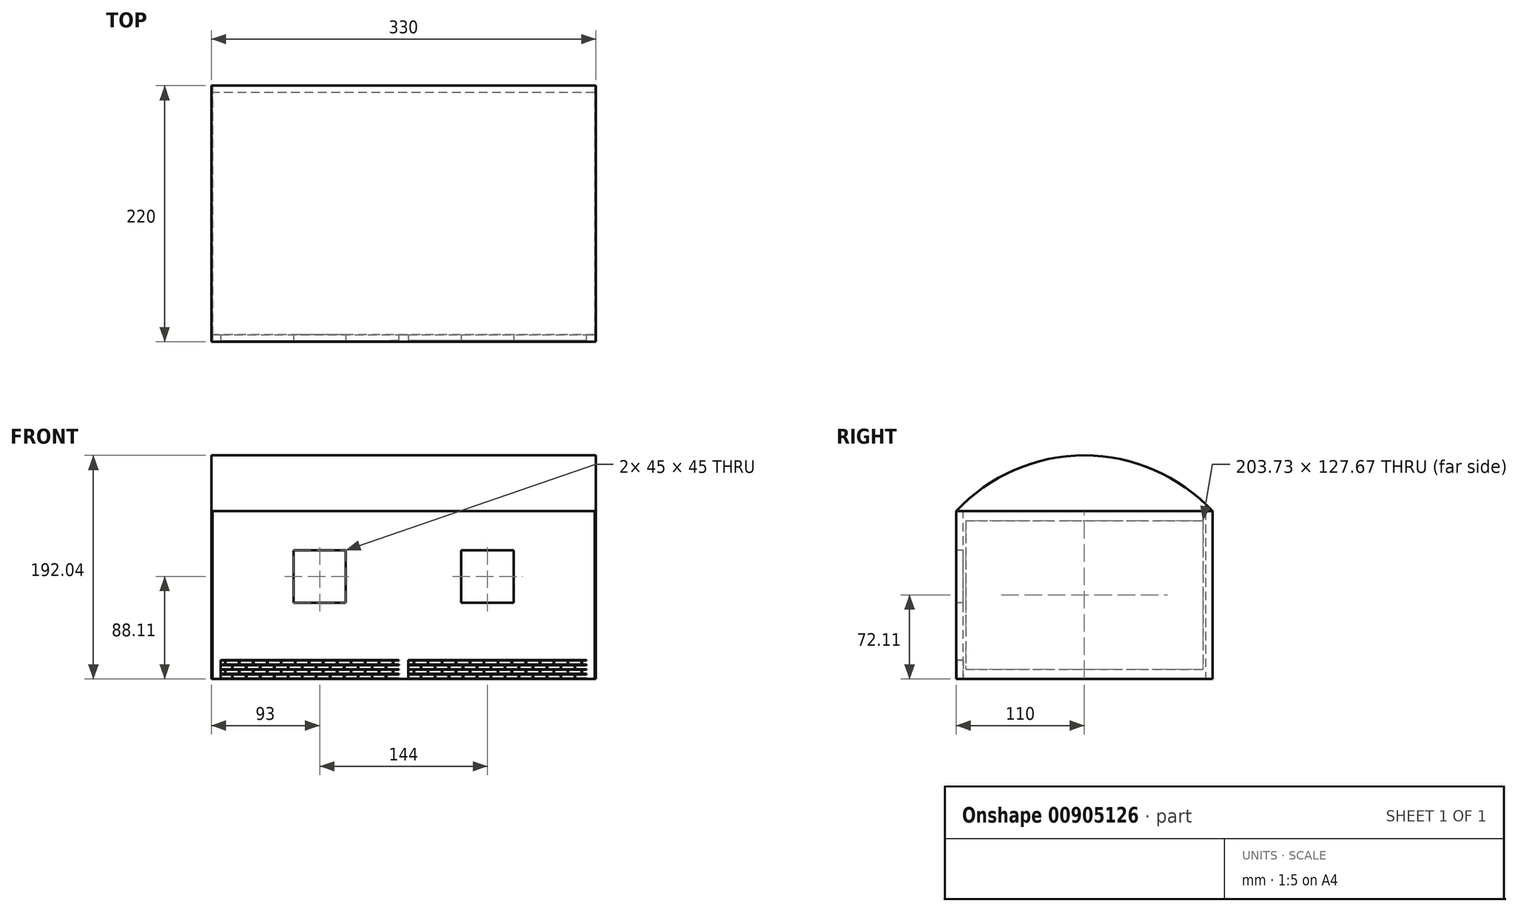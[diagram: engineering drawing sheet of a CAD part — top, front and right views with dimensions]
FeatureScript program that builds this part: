
annotation { "Feature Type Name" : "Feature", "Feature Type Description" : "" }
export const myFeature = defineFeature(function(context is Context, id is Id, definition is map)
    precondition{}
    {
        {
            var Q0;
            Q0=qCreatedBy(makeId("Front.planeOp"),FACE);
            var sketch = newSketch(context, id + "F0", { "sketchPlane" : qUnion([Q0])});
            skLineSegment(sketch, "E0", {"start": v(-165, -72) * mm, "end": v(165, -72) * mm});
            skLineSegment(sketch, "E1", {"start": v(-165, -72) * mm, "end": v(-165, 72) * mm});
            skLineSegment(sketch, "E2", {"start": v(165, -72) * mm, "end": v(165, 72) * mm});
            skLineSegment(sketch, "E3", {"start": v(165, 72) * mm, "end": v(-165, 72) * mm});
            skLineSegment(sketch, "E4", {"start": v(0, 72) * mm, "end": v(0, -56) * mm});
            skLineSegment(sketch, "E5", {"start": v(48, 72) * mm, "end": v(48, -56) * mm});
            skLineSegment(sketch, "E6", {"start": v(96, 72) * mm, "end": v(96, -56) * mm});
            skLineSegment(sketch, "E7", {"start": v(144, 72) * mm, "end": v(144, -56) * mm});
            skLineSegment(sketch, "E8", {"start": v(-48, 72) * mm, "end": v(-48, -56) * mm});
            skLineSegment(sketch, "E9", {"start": v(-96, 72) * mm, "end": v(-96, -56) * mm});
            skLineSegment(sketch, "E10", {"start": v(-144, 72) * mm, "end": v(-144, -56) * mm});
            skLineSegment(sketch, "E11", {"start": v(-165, -56) * mm, "end": v(165, -56) * mm});
            skLineSegment(sketch, "E12", {"start": v(-94.5, 38.5) * mm, "end": v(-49.5, 38.5) * mm});
            skLineSegment(sketch, "E13", {"start": v(-49.5, 38.5) * mm, "end": v(-49.5, -6.5) * mm});
            skLineSegment(sketch, "E14", {"start": v(-49.5, -6.5) * mm, "end": v(-94.5, -6.5) * mm});
            skLineSegment(sketch, "E15", {"start": v(-94.5, -6.5) * mm, "end": v(-94.5, 38.5) * mm});
            skLineSegment(sketch, "E16", {"start": v(49.5, 38.5) * mm, "end": v(94.5, 38.5) * mm});
            skLineSegment(sketch, "E17", {"start": v(94.5, 38.5) * mm, "end": v(94.5, -6.5) * mm});
            skLineSegment(sketch, "E18", {"start": v(94.5, -6.5) * mm, "end": v(49.5, -6.5) * mm});
            skLineSegment(sketch, "E19", {"start": v(49.5, -6.5) * mm, "end": v(49.5, 38.5) * mm});
            skLineSegment(sketch, "E20", {"start": v(-72, 38.5) * mm, "end": v(-72, -6.5) * mm});
            skLineSegment(sketch, "E21", {"start": v(72, 38.5) * mm, "end": v(72, -6.5) * mm});
            skLineSegment(sketch, "E22", {"start": v(-157, -56) * mm, "end": v(-157, -72) * mm});
            skLineSegment(sketch, "E23", {"start": v(-4, -56) * mm, "end": v(-4, -72) * mm});
            skLineSegment(sketch, "E24", {"start": v(-164, -72) * mm, "end": v(-164, 72) * mm});
            skLineSegment(sketch, "E25", {"start": v(164, -72) * mm, "end": v(164, 72) * mm});
            skLineSegment(sketch, "E26", {"start": v(-146.75, -68.25) * mm, "end": v(-135.25, -68.25) * mm});
            skLineSegment(sketch, "E27", {"start": v(-135.25, -68.25) * mm, "end": v(-135.25, -71.75) * mm});
            skLineSegment(sketch, "E28", {"start": v(-135.25, -71.75) * mm, "end": v(-146.75, -71.75) * mm});
            skLineSegment(sketch, "E29", {"start": v(-146.75, -71.75) * mm, "end": v(-146.75, -68.25) * mm});
            skLineSegment(sketch, "E30", {"start": v(-134.75, -68.25) * mm, "end": v(-123.25, -68.25) * mm});
            skLineSegment(sketch, "E31", {"start": v(-123.25, -68.25) * mm, "end": v(-123.25, -71.75) * mm});
            skLineSegment(sketch, "E32", {"start": v(-123.25, -71.75) * mm, "end": v(-134.75, -71.75) * mm});
            skLineSegment(sketch, "E33", {"start": v(-134.75, -71.75) * mm, "end": v(-134.75, -68.25) * mm});
            skLineSegment(sketch, "E34", {"start": v(-122.75, -68.25) * mm, "end": v(-111.25, -68.25) * mm});
            skLineSegment(sketch, "E35", {"start": v(-111.25, -68.25) * mm, "end": v(-111.25, -71.75) * mm});
            skLineSegment(sketch, "E36", {"start": v(-111.25, -71.75) * mm, "end": v(-122.75, -71.75) * mm});
            skLineSegment(sketch, "E37", {"start": v(-122.75, -71.75) * mm, "end": v(-122.75, -68.25) * mm});
            skLineSegment(sketch, "E38", {"start": v(-110.75, -68.25) * mm, "end": v(-99.25, -68.25) * mm});
            skLineSegment(sketch, "E39", {"start": v(-99.25, -68.25) * mm, "end": v(-99.25, -71.75) * mm});
            skLineSegment(sketch, "E40", {"start": v(-99.25, -71.75) * mm, "end": v(-110.75, -71.75) * mm});
            skLineSegment(sketch, "E41", {"start": v(-110.75, -71.75) * mm, "end": v(-110.75, -68.25) * mm});
            skLineSegment(sketch, "E42", {"start": v(-98.75, -68.25) * mm, "end": v(-87.25, -68.25) * mm});
            skLineSegment(sketch, "E43", {"start": v(-87.25, -68.25) * mm, "end": v(-87.25, -71.75) * mm});
            skLineSegment(sketch, "E44", {"start": v(-87.25, -71.75) * mm, "end": v(-98.75, -71.75) * mm});
            skLineSegment(sketch, "E45", {"start": v(-98.75, -71.75) * mm, "end": v(-98.75, -68.25) * mm});
            skLineSegment(sketch, "E46", {"start": v(-86.75, -68.25) * mm, "end": v(-75.25, -68.25) * mm});
            skLineSegment(sketch, "E47", {"start": v(-75.25, -68.25) * mm, "end": v(-75.25, -71.75) * mm});
            skLineSegment(sketch, "E48", {"start": v(-75.25, -71.75) * mm, "end": v(-86.75, -71.75) * mm});
            skLineSegment(sketch, "E49", {"start": v(-86.75, -71.75) * mm, "end": v(-86.75, -68.25) * mm});
            skLineSegment(sketch, "E50", {"start": v(-74.75, -68.25) * mm, "end": v(-63.25, -68.25) * mm});
            skLineSegment(sketch, "E51", {"start": v(-63.25, -68.25) * mm, "end": v(-63.25, -71.75) * mm});
            skLineSegment(sketch, "E52", {"start": v(-63.25, -71.75) * mm, "end": v(-74.75, -71.75) * mm});
            skLineSegment(sketch, "E53", {"start": v(-74.75, -71.75) * mm, "end": v(-74.75, -68.25) * mm});
            skLineSegment(sketch, "E54", {"start": v(-62.75, -68.25) * mm, "end": v(-51.25, -68.25) * mm});
            skLineSegment(sketch, "E55", {"start": v(-51.25, -68.25) * mm, "end": v(-51.25, -71.75) * mm});
            skLineSegment(sketch, "E56", {"start": v(-51.25, -71.75) * mm, "end": v(-62.75, -71.75) * mm});
            skLineSegment(sketch, "E57", {"start": v(-62.75, -71.75) * mm, "end": v(-62.75, -68.25) * mm});
            skLineSegment(sketch, "E58", {"start": v(-50.75, -68.25) * mm, "end": v(-39.25, -68.25) * mm});
            skLineSegment(sketch, "E59", {"start": v(-39.25, -68.25) * mm, "end": v(-39.25, -71.75) * mm});
            skLineSegment(sketch, "E60", {"start": v(-39.25, -71.75) * mm, "end": v(-50.75, -71.75) * mm});
            skLineSegment(sketch, "E61", {"start": v(-50.75, -71.75) * mm, "end": v(-50.75, -68.25) * mm});
            skLineSegment(sketch, "E62", {"start": v(-38.75, -68.25) * mm, "end": v(-27.25, -68.25) * mm});
            skLineSegment(sketch, "E63", {"start": v(-27.25, -68.25) * mm, "end": v(-27.25, -71.75) * mm});
            skLineSegment(sketch, "E64", {"start": v(-27.25, -71.75) * mm, "end": v(-38.75, -71.75) * mm});
            skLineSegment(sketch, "E65", {"start": v(-38.75, -71.75) * mm, "end": v(-38.75, -68.25) * mm});
            skLineSegment(sketch, "E66", {"start": v(-26.75, -68.25) * mm, "end": v(-15.25, -68.25) * mm});
            skLineSegment(sketch, "E67", {"start": v(-15.25, -68.25) * mm, "end": v(-15.25, -71.75) * mm});
            skLineSegment(sketch, "E68", {"start": v(-15.25, -71.75) * mm, "end": v(-26.75, -71.75) * mm});
            skLineSegment(sketch, "E69", {"start": v(-26.75, -71.75) * mm, "end": v(-26.75, -68.25) * mm});
            skLineSegment(sketch, "E70", {"start": v(-152.75, -64.25) * mm, "end": v(-141.25, -64.25) * mm});
            skLineSegment(sketch, "E71", {"start": v(-141.25, -64.25) * mm, "end": v(-141.25, -67.75) * mm});
            skLineSegment(sketch, "E72", {"start": v(-141.25, -67.75) * mm, "end": v(-152.75, -67.75) * mm});
            skLineSegment(sketch, "E73", {"start": v(-152.75, -67.75) * mm, "end": v(-152.75, -64.25) * mm});
            skLineSegment(sketch, "E74", {"start": v(-140.75, -64.25) * mm, "end": v(-129.25, -64.25) * mm});
            skLineSegment(sketch, "E75", {"start": v(-129.25, -64.25) * mm, "end": v(-129.25, -67.75) * mm});
            skLineSegment(sketch, "E76", {"start": v(-129.25, -67.75) * mm, "end": v(-140.75, -67.75) * mm});
            skLineSegment(sketch, "E77", {"start": v(-140.75, -67.75) * mm, "end": v(-140.75, -64.25) * mm});
            skLineSegment(sketch, "E78", {"start": v(-128.75, -64.25) * mm, "end": v(-117.25, -64.25) * mm});
            skLineSegment(sketch, "E79", {"start": v(-117.25, -64.25) * mm, "end": v(-117.25, -67.75) * mm});
            skLineSegment(sketch, "E80", {"start": v(-117.25, -67.75) * mm, "end": v(-128.75, -67.75) * mm});
            skLineSegment(sketch, "E81", {"start": v(-128.75, -67.75) * mm, "end": v(-128.75, -64.25) * mm});
            skLineSegment(sketch, "E82", {"start": v(-116.75, -64.25) * mm, "end": v(-105.25, -64.25) * mm});
            skLineSegment(sketch, "E83", {"start": v(-105.25, -64.25) * mm, "end": v(-105.25, -67.75) * mm});
            skLineSegment(sketch, "E84", {"start": v(-105.25, -67.75) * mm, "end": v(-116.75, -67.75) * mm});
            skLineSegment(sketch, "E85", {"start": v(-116.75, -67.75) * mm, "end": v(-116.75, -64.25) * mm});
            skLineSegment(sketch, "E86", {"start": v(-104.75, -64.25) * mm, "end": v(-93.25, -64.25) * mm});
            skLineSegment(sketch, "E87", {"start": v(-93.25, -64.25) * mm, "end": v(-93.25, -67.75) * mm});
            skLineSegment(sketch, "E88", {"start": v(-93.25, -67.75) * mm, "end": v(-104.75, -67.75) * mm});
            skLineSegment(sketch, "E89", {"start": v(-104.75, -67.75) * mm, "end": v(-104.75, -64.25) * mm});
            skLineSegment(sketch, "E90", {"start": v(-92.75, -64.25) * mm, "end": v(-81.25, -64.25) * mm});
            skLineSegment(sketch, "E91", {"start": v(-81.25, -64.25) * mm, "end": v(-81.25, -67.75) * mm});
            skLineSegment(sketch, "E92", {"start": v(-81.25, -67.75) * mm, "end": v(-92.75, -67.75) * mm});
            skLineSegment(sketch, "E93", {"start": v(-92.75, -67.75) * mm, "end": v(-92.75, -64.25) * mm});
            skLineSegment(sketch, "E94", {"start": v(-80.75, -64.25) * mm, "end": v(-69.25, -64.25) * mm});
            skLineSegment(sketch, "E95", {"start": v(-69.25, -64.25) * mm, "end": v(-69.25, -67.75) * mm});
            skLineSegment(sketch, "E96", {"start": v(-69.25, -67.75) * mm, "end": v(-80.75, -67.75) * mm});
            skLineSegment(sketch, "E97", {"start": v(-80.75, -67.75) * mm, "end": v(-80.75, -64.25) * mm});
            skLineSegment(sketch, "E98", {"start": v(-68.75, -64.25) * mm, "end": v(-57.25, -64.25) * mm});
            skLineSegment(sketch, "E99", {"start": v(-57.25, -64.25) * mm, "end": v(-57.25, -67.75) * mm});
            skLineSegment(sketch, "E100", {"start": v(-57.25, -67.75) * mm, "end": v(-68.75, -67.75) * mm});
            skLineSegment(sketch, "E101", {"start": v(-68.75, -67.75) * mm, "end": v(-68.75, -64.25) * mm});
            skLineSegment(sketch, "E102", {"start": v(-56.75, -64.25) * mm, "end": v(-45.25, -64.25) * mm});
            skLineSegment(sketch, "E103", {"start": v(-45.25, -64.25) * mm, "end": v(-45.25, -67.75) * mm});
            skLineSegment(sketch, "E104", {"start": v(-45.25, -67.75) * mm, "end": v(-56.75, -67.75) * mm});
            skLineSegment(sketch, "E105", {"start": v(-56.75, -67.75) * mm, "end": v(-56.75, -64.25) * mm});
            skLineSegment(sketch, "E106", {"start": v(-44.75, -64.25) * mm, "end": v(-33.25, -64.25) * mm});
            skLineSegment(sketch, "E107", {"start": v(-33.25, -64.25) * mm, "end": v(-33.25, -67.75) * mm});
            skLineSegment(sketch, "E108", {"start": v(-33.25, -67.75) * mm, "end": v(-44.75, -67.75) * mm});
            skLineSegment(sketch, "E109", {"start": v(-44.75, -67.75) * mm, "end": v(-44.75, -64.25) * mm});
            skLineSegment(sketch, "E110", {"start": v(-32.75, -64.25) * mm, "end": v(-21.25, -64.25) * mm});
            skLineSegment(sketch, "E111", {"start": v(-21.25, -64.25) * mm, "end": v(-21.25, -67.75) * mm});
            skLineSegment(sketch, "E112", {"start": v(-21.25, -67.75) * mm, "end": v(-32.75, -67.75) * mm});
            skLineSegment(sketch, "E113", {"start": v(-32.75, -67.75) * mm, "end": v(-32.75, -64.25) * mm});
            skLineSegment(sketch, "E114", {"start": v(-20.75, -64.25) * mm, "end": v(-9.25, -64.25) * mm});
            skLineSegment(sketch, "E115", {"start": v(-9.25, -64.25) * mm, "end": v(-9.25, -67.75) * mm});
            skLineSegment(sketch, "E116", {"start": v(-9.25, -67.75) * mm, "end": v(-20.75, -67.75) * mm});
            skLineSegment(sketch, "E117", {"start": v(-20.75, -67.75) * mm, "end": v(-20.75, -64.25) * mm});
            skLineSegment(sketch, "E118", {"start": v(-146.75, -60.25) * mm, "end": v(-135.25, -60.25) * mm});
            skLineSegment(sketch, "E119", {"start": v(-135.25, -60.25) * mm, "end": v(-135.25, -63.75) * mm});
            skLineSegment(sketch, "E120", {"start": v(-135.25, -63.75) * mm, "end": v(-146.75, -63.75) * mm});
            skLineSegment(sketch, "E121", {"start": v(-146.75, -63.75) * mm, "end": v(-146.75, -60.25) * mm});
            skLineSegment(sketch, "E122", {"start": v(-134.75, -60.25) * mm, "end": v(-123.25, -60.25) * mm});
            skLineSegment(sketch, "E123", {"start": v(-123.25, -60.25) * mm, "end": v(-123.25, -63.75) * mm});
            skLineSegment(sketch, "E124", {"start": v(-123.25, -63.75) * mm, "end": v(-134.75, -63.75) * mm});
            skLineSegment(sketch, "E125", {"start": v(-134.75, -63.75) * mm, "end": v(-134.75, -60.25) * mm});
            skLineSegment(sketch, "E126", {"start": v(-122.75, -60.25) * mm, "end": v(-111.25, -60.25) * mm});
            skLineSegment(sketch, "E127", {"start": v(-111.25, -60.25) * mm, "end": v(-111.25, -63.75) * mm});
            skLineSegment(sketch, "E128", {"start": v(-111.25, -63.75) * mm, "end": v(-122.75, -63.75) * mm});
            skLineSegment(sketch, "E129", {"start": v(-122.75, -63.75) * mm, "end": v(-122.75, -60.25) * mm});
            skLineSegment(sketch, "E130", {"start": v(-110.75, -60.25) * mm, "end": v(-99.25, -60.25) * mm});
            skLineSegment(sketch, "E131", {"start": v(-99.25, -60.25) * mm, "end": v(-99.25, -63.75) * mm});
            skLineSegment(sketch, "E132", {"start": v(-99.25, -63.75) * mm, "end": v(-110.75, -63.75) * mm});
            skLineSegment(sketch, "E133", {"start": v(-110.75, -63.75) * mm, "end": v(-110.75, -60.25) * mm});
            skLineSegment(sketch, "E134", {"start": v(-98.75, -60.25) * mm, "end": v(-87.25, -60.25) * mm});
            skLineSegment(sketch, "E135", {"start": v(-87.25, -60.25) * mm, "end": v(-87.25, -63.75) * mm});
            skLineSegment(sketch, "E136", {"start": v(-87.25, -63.75) * mm, "end": v(-98.75, -63.75) * mm});
            skLineSegment(sketch, "E137", {"start": v(-98.75, -63.75) * mm, "end": v(-98.75, -60.25) * mm});
            skLineSegment(sketch, "E138", {"start": v(-86.75, -60.25) * mm, "end": v(-75.25, -60.25) * mm});
            skLineSegment(sketch, "E139", {"start": v(-75.25, -60.25) * mm, "end": v(-75.25, -63.75) * mm});
            skLineSegment(sketch, "E140", {"start": v(-75.25, -63.75) * mm, "end": v(-86.75, -63.75) * mm});
            skLineSegment(sketch, "E141", {"start": v(-86.75, -63.75) * mm, "end": v(-86.75, -60.25) * mm});
            skLineSegment(sketch, "E142", {"start": v(-74.75, -60.25) * mm, "end": v(-63.25, -60.25) * mm});
            skLineSegment(sketch, "E143", {"start": v(-63.25, -60.25) * mm, "end": v(-63.25, -63.75) * mm});
            skLineSegment(sketch, "E144", {"start": v(-63.25, -63.75) * mm, "end": v(-74.75, -63.75) * mm});
            skLineSegment(sketch, "E145", {"start": v(-74.75, -63.75) * mm, "end": v(-74.75, -60.25) * mm});
            skLineSegment(sketch, "E146", {"start": v(-62.75, -60.25) * mm, "end": v(-51.25, -60.25) * mm});
            skLineSegment(sketch, "E147", {"start": v(-51.25, -60.25) * mm, "end": v(-51.25, -63.75) * mm});
            skLineSegment(sketch, "E148", {"start": v(-51.25, -63.75) * mm, "end": v(-62.75, -63.75) * mm});
            skLineSegment(sketch, "E149", {"start": v(-62.75, -63.75) * mm, "end": v(-62.75, -60.25) * mm});
            skLineSegment(sketch, "E150", {"start": v(-50.75, -60.25) * mm, "end": v(-39.25, -60.25) * mm});
            skLineSegment(sketch, "E151", {"start": v(-39.25, -60.25) * mm, "end": v(-39.25, -63.75) * mm});
            skLineSegment(sketch, "E152", {"start": v(-39.25, -63.75) * mm, "end": v(-50.75, -63.75) * mm});
            skLineSegment(sketch, "E153", {"start": v(-50.75, -63.75) * mm, "end": v(-50.75, -60.25) * mm});
            skLineSegment(sketch, "E154", {"start": v(-38.75, -60.25) * mm, "end": v(-27.25, -60.25) * mm});
            skLineSegment(sketch, "E155", {"start": v(-27.25, -60.25) * mm, "end": v(-27.25, -63.75) * mm});
            skLineSegment(sketch, "E156", {"start": v(-27.25, -63.75) * mm, "end": v(-38.75, -63.75) * mm});
            skLineSegment(sketch, "E157", {"start": v(-38.75, -63.75) * mm, "end": v(-38.75, -60.25) * mm});
            skLineSegment(sketch, "E158", {"start": v(-26.75, -60.25) * mm, "end": v(-15.25, -60.25) * mm});
            skLineSegment(sketch, "E159", {"start": v(-15.25, -60.25) * mm, "end": v(-15.25, -63.75) * mm});
            skLineSegment(sketch, "E160", {"start": v(-15.25, -63.75) * mm, "end": v(-26.75, -63.75) * mm});
            skLineSegment(sketch, "E161", {"start": v(-26.75, -63.75) * mm, "end": v(-26.75, -60.25) * mm});
            skLineSegment(sketch, "E162", {"start": v(-152.75, -56.25) * mm, "end": v(-141.25, -56.25) * mm});
            skLineSegment(sketch, "E163", {"start": v(-141.25, -56.25) * mm, "end": v(-141.25, -59.75) * mm});
            skLineSegment(sketch, "E164", {"start": v(-141.25, -59.75) * mm, "end": v(-152.75, -59.75) * mm});
            skLineSegment(sketch, "E165", {"start": v(-152.75, -59.75) * mm, "end": v(-152.75, -56.25) * mm});
            skLineSegment(sketch, "E166", {"start": v(-140.75, -56.25) * mm, "end": v(-129.25, -56.25) * mm});
            skLineSegment(sketch, "E167", {"start": v(-129.25, -56.25) * mm, "end": v(-129.25, -59.75) * mm});
            skLineSegment(sketch, "E168", {"start": v(-129.25, -59.75) * mm, "end": v(-140.75, -59.75) * mm});
            skLineSegment(sketch, "E169", {"start": v(-140.75, -59.75) * mm, "end": v(-140.75, -56.25) * mm});
            skLineSegment(sketch, "E170", {"start": v(-128.75, -56.25) * mm, "end": v(-117.25, -56.25) * mm});
            skLineSegment(sketch, "E171", {"start": v(-117.25, -56.25) * mm, "end": v(-117.25, -59.75) * mm});
            skLineSegment(sketch, "E172", {"start": v(-117.25, -59.75) * mm, "end": v(-128.75, -59.75) * mm});
            skLineSegment(sketch, "E173", {"start": v(-128.75, -59.75) * mm, "end": v(-128.75, -56.25) * mm});
            skLineSegment(sketch, "E174", {"start": v(-116.75, -56.25) * mm, "end": v(-105.25, -56.25) * mm});
            skLineSegment(sketch, "E175", {"start": v(-105.25, -56.25) * mm, "end": v(-105.25, -59.75) * mm});
            skLineSegment(sketch, "E176", {"start": v(-105.25, -59.75) * mm, "end": v(-116.75, -59.75) * mm});
            skLineSegment(sketch, "E177", {"start": v(-116.75, -59.75) * mm, "end": v(-116.75, -56.25) * mm});
            skLineSegment(sketch, "E178", {"start": v(-104.75, -56.25) * mm, "end": v(-93.25, -56.25) * mm});
            skLineSegment(sketch, "E179", {"start": v(-93.25, -56.25) * mm, "end": v(-93.25, -59.75) * mm});
            skLineSegment(sketch, "E180", {"start": v(-93.25, -59.75) * mm, "end": v(-104.75, -59.75) * mm});
            skLineSegment(sketch, "E181", {"start": v(-104.75, -59.75) * mm, "end": v(-104.75, -56.25) * mm});
            skLineSegment(sketch, "E182", {"start": v(-92.75, -56.25) * mm, "end": v(-81.25, -56.25) * mm});
            skLineSegment(sketch, "E183", {"start": v(-81.25, -56.25) * mm, "end": v(-81.25, -59.75) * mm});
            skLineSegment(sketch, "E184", {"start": v(-81.25, -59.75) * mm, "end": v(-92.75, -59.75) * mm});
            skLineSegment(sketch, "E185", {"start": v(-92.75, -59.75) * mm, "end": v(-92.75, -56.25) * mm});
            skLineSegment(sketch, "E186", {"start": v(-80.75, -56.25) * mm, "end": v(-69.25, -56.25) * mm});
            skLineSegment(sketch, "E187", {"start": v(-69.25, -56.25) * mm, "end": v(-69.25, -59.75) * mm});
            skLineSegment(sketch, "E188", {"start": v(-69.25, -59.75) * mm, "end": v(-80.75, -59.75) * mm});
            skLineSegment(sketch, "E189", {"start": v(-80.75, -59.75) * mm, "end": v(-80.75, -56.25) * mm});
            skLineSegment(sketch, "E190", {"start": v(-68.75, -56.25) * mm, "end": v(-57.25, -56.25) * mm});
            skLineSegment(sketch, "E191", {"start": v(-57.25, -56.25) * mm, "end": v(-57.25, -59.75) * mm});
            skLineSegment(sketch, "E192", {"start": v(-57.25, -59.75) * mm, "end": v(-68.75, -59.75) * mm});
            skLineSegment(sketch, "E193", {"start": v(-68.75, -59.75) * mm, "end": v(-68.75, -56.25) * mm});
            skLineSegment(sketch, "E194", {"start": v(-56.75, -56.25) * mm, "end": v(-45.25, -56.25) * mm});
            skLineSegment(sketch, "E195", {"start": v(-45.25, -56.25) * mm, "end": v(-45.25, -59.75) * mm});
            skLineSegment(sketch, "E196", {"start": v(-45.25, -59.75) * mm, "end": v(-56.75, -59.75) * mm});
            skLineSegment(sketch, "E197", {"start": v(-56.75, -59.75) * mm, "end": v(-56.75, -56.25) * mm});
            skLineSegment(sketch, "E198", {"start": v(-44.75, -56.25) * mm, "end": v(-33.25, -56.25) * mm});
            skLineSegment(sketch, "E199", {"start": v(-33.25, -56.25) * mm, "end": v(-33.25, -59.75) * mm});
            skLineSegment(sketch, "E200", {"start": v(-33.25, -59.75) * mm, "end": v(-44.75, -59.75) * mm});
            skLineSegment(sketch, "E201", {"start": v(-44.75, -59.75) * mm, "end": v(-44.75, -56.25) * mm});
            skLineSegment(sketch, "E202", {"start": v(-32.75, -56.25) * mm, "end": v(-21.25, -56.25) * mm});
            skLineSegment(sketch, "E203", {"start": v(-21.25, -56.25) * mm, "end": v(-21.25, -59.75) * mm});
            skLineSegment(sketch, "E204", {"start": v(-21.25, -59.75) * mm, "end": v(-32.75, -59.75) * mm});
            skLineSegment(sketch, "E205", {"start": v(-32.75, -59.75) * mm, "end": v(-32.75, -56.25) * mm});
            skLineSegment(sketch, "E206", {"start": v(-20.75, -56.25) * mm, "end": v(-9.25, -56.25) * mm});
            skLineSegment(sketch, "E207", {"start": v(-9.25, -56.25) * mm, "end": v(-9.25, -59.75) * mm});
            skLineSegment(sketch, "E208", {"start": v(-9.25, -59.75) * mm, "end": v(-20.75, -59.75) * mm});
            skLineSegment(sketch, "E209", {"start": v(-20.75, -59.75) * mm, "end": v(-20.75, -56.25) * mm});
            skLineSegment(sketch, "E210", {"start": v(-4, -67.75) * mm, "end": v(-8.75, -67.75) * mm});
            skLineSegment(sketch, "E211", {"start": v(-8.75, -67.75) * mm, "end": v(-8.75, -64.25) * mm});
            skLineSegment(sketch, "E212", {"start": v(-8.75, -64.25) * mm, "end": v(-4, -64.25) * mm});
            skLineSegment(sketch, "E213", {"start": v(-4, -71.75) * mm, "end": v(-14.75, -71.75) * mm});
            skLineSegment(sketch, "E214", {"start": v(-14.75, -71.75) * mm, "end": v(-14.75, -68.25) * mm});
            skLineSegment(sketch, "E215", {"start": v(-14.75, -68.25) * mm, "end": v(-4, -68.25) * mm});
            skLineSegment(sketch, "E216", {"start": v(-4, -63.75) * mm, "end": v(-14.75, -63.75) * mm});
            skLineSegment(sketch, "E217", {"start": v(-14.75, -63.75) * mm, "end": v(-14.75, -60.25) * mm});
            skLineSegment(sketch, "E218", {"start": v(-14.75, -60.25) * mm, "end": v(-4, -60.25) * mm});
            skLineSegment(sketch, "E219", {"start": v(-4, -59.75) * mm, "end": v(-8.75, -59.75) * mm});
            skLineSegment(sketch, "E220", {"start": v(-8.75, -59.75) * mm, "end": v(-8.75, -56.25) * mm});
            skLineSegment(sketch, "E221", {"start": v(-8.75, -56.25) * mm, "end": v(-4, -56.25) * mm});
            skLineSegment(sketch, "E222", {"start": v(-157, -56.25) * mm, "end": v(-153.25, -56.25) * mm});
            skLineSegment(sketch, "E223", {"start": v(-153.25, -56.25) * mm, "end": v(-153.25, -59.75) * mm});
            skLineSegment(sketch, "E224", {"start": v(-153.25, -59.75) * mm, "end": v(-157, -59.75) * mm});
            skLineSegment(sketch, "E225", {"start": v(-157, -60.25) * mm, "end": v(-147.25, -60.25) * mm});
            skLineSegment(sketch, "E226", {"start": v(-147.25, -60.25) * mm, "end": v(-147.25, -63.75) * mm});
            skLineSegment(sketch, "E227", {"start": v(-147.25, -63.75) * mm, "end": v(-157, -63.75) * mm});
            skLineSegment(sketch, "E228", {"start": v(-157, -64.25) * mm, "end": v(-153.25, -64.25) * mm});
            skLineSegment(sketch, "E229", {"start": v(-153.25, -64.25) * mm, "end": v(-153.25, -67.75) * mm});
            skLineSegment(sketch, "E230", {"start": v(-153.25, -67.75) * mm, "end": v(-157, -67.75) * mm});
            skLineSegment(sketch, "E231", {"start": v(-157, -68.25) * mm, "end": v(-147.25, -68.25) * mm});
            skLineSegment(sketch, "E232", {"start": v(-147.25, -68.25) * mm, "end": v(-147.25, -71.75) * mm});
            skLineSegment(sketch, "E233", {"start": v(-147.25, -71.75) * mm, "end": v(-157, -71.75) * mm});
            skLineSegment(sketch, "E234", {"start": v(157, -56) * mm, "end": v(157, -72) * mm});
            skLineSegment(sketch, "E235", {"start": v(4, -56) * mm, "end": v(4, -72) * mm});
            skLineSegment(sketch, "E236", {"start": v(146.75, -68.25) * mm, "end": v(135.25, -68.25) * mm});
            skLineSegment(sketch, "E237", {"start": v(135.25, -68.25) * mm, "end": v(135.25, -71.75) * mm});
            skLineSegment(sketch, "E238", {"start": v(135.25, -71.75) * mm, "end": v(146.75, -71.75) * mm});
            skLineSegment(sketch, "E239", {"start": v(146.75, -71.75) * mm, "end": v(146.75, -68.25) * mm});
            skLineSegment(sketch, "E240", {"start": v(134.75, -68.25) * mm, "end": v(123.25, -68.25) * mm});
            skLineSegment(sketch, "E241", {"start": v(123.25, -68.25) * mm, "end": v(123.25, -71.75) * mm});
            skLineSegment(sketch, "E242", {"start": v(123.25, -71.75) * mm, "end": v(134.75, -71.75) * mm});
            skLineSegment(sketch, "E243", {"start": v(134.75, -71.75) * mm, "end": v(134.75, -68.25) * mm});
            skLineSegment(sketch, "E244", {"start": v(122.75, -68.25) * mm, "end": v(111.25, -68.25) * mm});
            skLineSegment(sketch, "E245", {"start": v(111.25, -68.25) * mm, "end": v(111.25, -71.75) * mm});
            skLineSegment(sketch, "E246", {"start": v(111.25, -71.75) * mm, "end": v(122.75, -71.75) * mm});
            skLineSegment(sketch, "E247", {"start": v(122.75, -71.75) * mm, "end": v(122.75, -68.25) * mm});
            skLineSegment(sketch, "E248", {"start": v(110.75, -68.25) * mm, "end": v(99.25, -68.25) * mm});
            skLineSegment(sketch, "E249", {"start": v(99.25, -68.25) * mm, "end": v(99.25, -71.75) * mm});
            skLineSegment(sketch, "E250", {"start": v(99.25, -71.75) * mm, "end": v(110.75, -71.75) * mm});
            skLineSegment(sketch, "E251", {"start": v(110.75, -71.75) * mm, "end": v(110.75, -68.25) * mm});
            skLineSegment(sketch, "E252", {"start": v(98.75, -68.25) * mm, "end": v(87.25, -68.25) * mm});
            skLineSegment(sketch, "E253", {"start": v(87.25, -68.25) * mm, "end": v(87.25, -71.75) * mm});
            skLineSegment(sketch, "E254", {"start": v(87.25, -71.75) * mm, "end": v(98.75, -71.75) * mm});
            skLineSegment(sketch, "E255", {"start": v(98.75, -71.75) * mm, "end": v(98.75, -68.25) * mm});
            skLineSegment(sketch, "E256", {"start": v(86.75, -68.25) * mm, "end": v(75.25, -68.25) * mm});
            skLineSegment(sketch, "E257", {"start": v(75.25, -68.25) * mm, "end": v(75.25, -71.75) * mm});
            skLineSegment(sketch, "E258", {"start": v(75.25, -71.75) * mm, "end": v(86.75, -71.75) * mm});
            skLineSegment(sketch, "E259", {"start": v(86.75, -71.75) * mm, "end": v(86.75, -68.25) * mm});
            skLineSegment(sketch, "E260", {"start": v(74.75, -68.25) * mm, "end": v(63.25, -68.25) * mm});
            skLineSegment(sketch, "E261", {"start": v(63.25, -68.25) * mm, "end": v(63.25, -71.75) * mm});
            skLineSegment(sketch, "E262", {"start": v(63.25, -71.75) * mm, "end": v(74.75, -71.75) * mm});
            skLineSegment(sketch, "E263", {"start": v(74.75, -71.75) * mm, "end": v(74.75, -68.25) * mm});
            skLineSegment(sketch, "E264", {"start": v(62.75, -68.25) * mm, "end": v(51.25, -68.25) * mm});
            skLineSegment(sketch, "E265", {"start": v(51.25, -68.25) * mm, "end": v(51.25, -71.75) * mm});
            skLineSegment(sketch, "E266", {"start": v(51.25, -71.75) * mm, "end": v(62.75, -71.75) * mm});
            skLineSegment(sketch, "E267", {"start": v(62.75, -71.75) * mm, "end": v(62.75, -68.25) * mm});
            skLineSegment(sketch, "E268", {"start": v(50.75, -68.25) * mm, "end": v(39.25, -68.25) * mm});
            skLineSegment(sketch, "E269", {"start": v(39.25, -68.25) * mm, "end": v(39.25, -71.75) * mm});
            skLineSegment(sketch, "E270", {"start": v(39.25, -71.75) * mm, "end": v(50.75, -71.75) * mm});
            skLineSegment(sketch, "E271", {"start": v(50.75, -71.75) * mm, "end": v(50.75, -68.25) * mm});
            skLineSegment(sketch, "E272", {"start": v(38.75, -68.25) * mm, "end": v(27.25, -68.25) * mm});
            skLineSegment(sketch, "E273", {"start": v(27.25, -68.25) * mm, "end": v(27.25, -71.75) * mm});
            skLineSegment(sketch, "E274", {"start": v(27.25, -71.75) * mm, "end": v(38.75, -71.75) * mm});
            skLineSegment(sketch, "E275", {"start": v(38.75, -71.75) * mm, "end": v(38.75, -68.25) * mm});
            skLineSegment(sketch, "E276", {"start": v(26.75, -68.25) * mm, "end": v(15.25, -68.25) * mm});
            skLineSegment(sketch, "E277", {"start": v(15.25, -68.25) * mm, "end": v(15.25, -71.75) * mm});
            skLineSegment(sketch, "E278", {"start": v(15.25, -71.75) * mm, "end": v(26.75, -71.75) * mm});
            skLineSegment(sketch, "E279", {"start": v(26.75, -71.75) * mm, "end": v(26.75, -68.25) * mm});
            skLineSegment(sketch, "E280", {"start": v(152.75, -64.25) * mm, "end": v(141.25, -64.25) * mm});
            skLineSegment(sketch, "E281", {"start": v(141.25, -64.25) * mm, "end": v(141.25, -67.75) * mm});
            skLineSegment(sketch, "E282", {"start": v(141.25, -67.75) * mm, "end": v(152.75, -67.75) * mm});
            skLineSegment(sketch, "E283", {"start": v(152.75, -67.75) * mm, "end": v(152.75, -64.25) * mm});
            skLineSegment(sketch, "E284", {"start": v(140.75, -64.25) * mm, "end": v(129.25, -64.25) * mm});
            skLineSegment(sketch, "E285", {"start": v(129.25, -64.25) * mm, "end": v(129.25, -67.75) * mm});
            skLineSegment(sketch, "E286", {"start": v(129.25, -67.75) * mm, "end": v(140.75, -67.75) * mm});
            skLineSegment(sketch, "E287", {"start": v(140.75, -67.75) * mm, "end": v(140.75, -64.25) * mm});
            skLineSegment(sketch, "E288", {"start": v(128.75, -64.25) * mm, "end": v(117.25, -64.25) * mm});
            skLineSegment(sketch, "E289", {"start": v(117.25, -64.25) * mm, "end": v(117.25, -67.75) * mm});
            skLineSegment(sketch, "E290", {"start": v(117.25, -67.75) * mm, "end": v(128.75, -67.75) * mm});
            skLineSegment(sketch, "E291", {"start": v(128.75, -67.75) * mm, "end": v(128.75, -64.25) * mm});
            skLineSegment(sketch, "E292", {"start": v(116.75, -64.25) * mm, "end": v(105.25, -64.25) * mm});
            skLineSegment(sketch, "E293", {"start": v(105.25, -64.25) * mm, "end": v(105.25, -67.75) * mm});
            skLineSegment(sketch, "E294", {"start": v(105.25, -67.75) * mm, "end": v(116.75, -67.75) * mm});
            skLineSegment(sketch, "E295", {"start": v(116.75, -67.75) * mm, "end": v(116.75, -64.25) * mm});
            skLineSegment(sketch, "E296", {"start": v(104.75, -64.25) * mm, "end": v(93.25, -64.25) * mm});
            skLineSegment(sketch, "E297", {"start": v(93.25, -64.25) * mm, "end": v(93.25, -67.75) * mm});
            skLineSegment(sketch, "E298", {"start": v(93.25, -67.75) * mm, "end": v(104.75, -67.75) * mm});
            skLineSegment(sketch, "E299", {"start": v(104.75, -67.75) * mm, "end": v(104.75, -64.25) * mm});
            skLineSegment(sketch, "E300", {"start": v(92.75, -64.25) * mm, "end": v(81.25, -64.25) * mm});
            skLineSegment(sketch, "E301", {"start": v(81.25, -64.25) * mm, "end": v(81.25, -67.75) * mm});
            skLineSegment(sketch, "E302", {"start": v(81.25, -67.75) * mm, "end": v(92.75, -67.75) * mm});
            skLineSegment(sketch, "E303", {"start": v(92.75, -67.75) * mm, "end": v(92.75, -64.25) * mm});
            skLineSegment(sketch, "E304", {"start": v(80.75, -64.25) * mm, "end": v(69.25, -64.25) * mm});
            skLineSegment(sketch, "E305", {"start": v(69.25, -64.25) * mm, "end": v(69.25, -67.75) * mm});
            skLineSegment(sketch, "E306", {"start": v(69.25, -67.75) * mm, "end": v(80.75, -67.75) * mm});
            skLineSegment(sketch, "E307", {"start": v(80.75, -67.75) * mm, "end": v(80.75, -64.25) * mm});
            skLineSegment(sketch, "E308", {"start": v(68.75, -64.25) * mm, "end": v(57.25, -64.25) * mm});
            skLineSegment(sketch, "E309", {"start": v(57.25, -64.25) * mm, "end": v(57.25, -67.75) * mm});
            skLineSegment(sketch, "E310", {"start": v(57.25, -67.75) * mm, "end": v(68.75, -67.75) * mm});
            skLineSegment(sketch, "E311", {"start": v(68.75, -67.75) * mm, "end": v(68.75, -64.25) * mm});
            skLineSegment(sketch, "E312", {"start": v(56.75, -64.25) * mm, "end": v(45.25, -64.25) * mm});
            skLineSegment(sketch, "E313", {"start": v(45.25, -64.25) * mm, "end": v(45.25, -67.75) * mm});
            skLineSegment(sketch, "E314", {"start": v(45.25, -67.75) * mm, "end": v(56.75, -67.75) * mm});
            skLineSegment(sketch, "E315", {"start": v(56.75, -67.75) * mm, "end": v(56.75, -64.25) * mm});
            skLineSegment(sketch, "E316", {"start": v(44.75, -64.25) * mm, "end": v(33.25, -64.25) * mm});
            skLineSegment(sketch, "E317", {"start": v(33.25, -64.25) * mm, "end": v(33.25, -67.75) * mm});
            skLineSegment(sketch, "E318", {"start": v(33.25, -67.75) * mm, "end": v(44.75, -67.75) * mm});
            skLineSegment(sketch, "E319", {"start": v(44.75, -67.75) * mm, "end": v(44.75, -64.25) * mm});
            skLineSegment(sketch, "E320", {"start": v(32.75, -64.25) * mm, "end": v(21.25, -64.25) * mm});
            skLineSegment(sketch, "E321", {"start": v(21.25, -64.25) * mm, "end": v(21.25, -67.75) * mm});
            skLineSegment(sketch, "E322", {"start": v(21.25, -67.75) * mm, "end": v(32.75, -67.75) * mm});
            skLineSegment(sketch, "E323", {"start": v(32.75, -67.75) * mm, "end": v(32.75, -64.25) * mm});
            skLineSegment(sketch, "E324", {"start": v(20.75, -64.25) * mm, "end": v(9.25, -64.25) * mm});
            skLineSegment(sketch, "E325", {"start": v(9.25, -64.25) * mm, "end": v(9.25, -67.75) * mm});
            skLineSegment(sketch, "E326", {"start": v(9.25, -67.75) * mm, "end": v(20.75, -67.75) * mm});
            skLineSegment(sketch, "E327", {"start": v(20.75, -67.75) * mm, "end": v(20.75, -64.25) * mm});
            skLineSegment(sketch, "E328", {"start": v(146.75, -60.25) * mm, "end": v(135.25, -60.25) * mm});
            skLineSegment(sketch, "E329", {"start": v(135.25, -60.25) * mm, "end": v(135.25, -63.75) * mm});
            skLineSegment(sketch, "E330", {"start": v(135.25, -63.75) * mm, "end": v(146.75, -63.75) * mm});
            skLineSegment(sketch, "E331", {"start": v(146.75, -63.75) * mm, "end": v(146.75, -60.25) * mm});
            skLineSegment(sketch, "E332", {"start": v(134.75, -60.25) * mm, "end": v(123.25, -60.25) * mm});
            skLineSegment(sketch, "E333", {"start": v(123.25, -60.25) * mm, "end": v(123.25, -63.75) * mm});
            skLineSegment(sketch, "E334", {"start": v(123.25, -63.75) * mm, "end": v(134.75, -63.75) * mm});
            skLineSegment(sketch, "E335", {"start": v(134.75, -63.75) * mm, "end": v(134.75, -60.25) * mm});
            skLineSegment(sketch, "E336", {"start": v(122.75, -60.25) * mm, "end": v(111.25, -60.25) * mm});
            skLineSegment(sketch, "E337", {"start": v(111.25, -60.25) * mm, "end": v(111.25, -63.75) * mm});
            skLineSegment(sketch, "E338", {"start": v(111.25, -63.75) * mm, "end": v(122.75, -63.75) * mm});
            skLineSegment(sketch, "E339", {"start": v(122.75, -63.75) * mm, "end": v(122.75, -60.25) * mm});
            skLineSegment(sketch, "E340", {"start": v(110.75, -60.25) * mm, "end": v(99.25, -60.25) * mm});
            skLineSegment(sketch, "E341", {"start": v(99.25, -60.25) * mm, "end": v(99.25, -63.75) * mm});
            skLineSegment(sketch, "E342", {"start": v(99.25, -63.75) * mm, "end": v(110.75, -63.75) * mm});
            skLineSegment(sketch, "E343", {"start": v(110.75, -63.75) * mm, "end": v(110.75, -60.25) * mm});
            skLineSegment(sketch, "E344", {"start": v(98.75, -60.25) * mm, "end": v(87.25, -60.25) * mm});
            skLineSegment(sketch, "E345", {"start": v(87.25, -60.25) * mm, "end": v(87.25, -63.75) * mm});
            skLineSegment(sketch, "E346", {"start": v(87.25, -63.75) * mm, "end": v(98.75, -63.75) * mm});
            skLineSegment(sketch, "E347", {"start": v(98.75, -63.75) * mm, "end": v(98.75, -60.25) * mm});
            skLineSegment(sketch, "E348", {"start": v(86.75, -60.25) * mm, "end": v(75.25, -60.25) * mm});
            skLineSegment(sketch, "E349", {"start": v(75.25, -60.25) * mm, "end": v(75.25, -63.75) * mm});
            skLineSegment(sketch, "E350", {"start": v(75.25, -63.75) * mm, "end": v(86.75, -63.75) * mm});
            skLineSegment(sketch, "E351", {"start": v(86.75, -63.75) * mm, "end": v(86.75, -60.25) * mm});
            skLineSegment(sketch, "E352", {"start": v(74.75, -60.25) * mm, "end": v(63.25, -60.25) * mm});
            skLineSegment(sketch, "E353", {"start": v(63.25, -60.25) * mm, "end": v(63.25, -63.75) * mm});
            skLineSegment(sketch, "E354", {"start": v(63.25, -63.75) * mm, "end": v(74.75, -63.75) * mm});
            skLineSegment(sketch, "E355", {"start": v(74.75, -63.75) * mm, "end": v(74.75, -60.25) * mm});
            skLineSegment(sketch, "E356", {"start": v(62.75, -60.25) * mm, "end": v(51.25, -60.25) * mm});
            skLineSegment(sketch, "E357", {"start": v(51.25, -60.25) * mm, "end": v(51.25, -63.75) * mm});
            skLineSegment(sketch, "E358", {"start": v(51.25, -63.75) * mm, "end": v(62.75, -63.75) * mm});
            skLineSegment(sketch, "E359", {"start": v(62.75, -63.75) * mm, "end": v(62.75, -60.25) * mm});
            skLineSegment(sketch, "E360", {"start": v(50.75, -60.25) * mm, "end": v(39.25, -60.25) * mm});
            skLineSegment(sketch, "E361", {"start": v(39.25, -60.25) * mm, "end": v(39.25, -63.75) * mm});
            skLineSegment(sketch, "E362", {"start": v(39.25, -63.75) * mm, "end": v(50.75, -63.75) * mm});
            skLineSegment(sketch, "E363", {"start": v(50.75, -63.75) * mm, "end": v(50.75, -60.25) * mm});
            skLineSegment(sketch, "E364", {"start": v(38.75, -60.25) * mm, "end": v(27.25, -60.25) * mm});
            skLineSegment(sketch, "E365", {"start": v(27.25, -60.25) * mm, "end": v(27.25, -63.75) * mm});
            skLineSegment(sketch, "E366", {"start": v(27.25, -63.75) * mm, "end": v(38.75, -63.75) * mm});
            skLineSegment(sketch, "E367", {"start": v(38.75, -63.75) * mm, "end": v(38.75, -60.25) * mm});
            skLineSegment(sketch, "E368", {"start": v(26.75, -60.25) * mm, "end": v(15.25, -60.25) * mm});
            skLineSegment(sketch, "E369", {"start": v(15.25, -60.25) * mm, "end": v(15.25, -63.75) * mm});
            skLineSegment(sketch, "E370", {"start": v(15.25, -63.75) * mm, "end": v(26.75, -63.75) * mm});
            skLineSegment(sketch, "E371", {"start": v(26.75, -63.75) * mm, "end": v(26.75, -60.25) * mm});
            skLineSegment(sketch, "E372", {"start": v(152.75, -56.25) * mm, "end": v(141.25, -56.25) * mm});
            skLineSegment(sketch, "E373", {"start": v(141.25, -56.25) * mm, "end": v(141.25, -59.75) * mm});
            skLineSegment(sketch, "E374", {"start": v(141.25, -59.75) * mm, "end": v(152.75, -59.75) * mm});
            skLineSegment(sketch, "E375", {"start": v(152.75, -59.75) * mm, "end": v(152.75, -56.25) * mm});
            skLineSegment(sketch, "E376", {"start": v(140.75, -56.25) * mm, "end": v(129.25, -56.25) * mm});
            skLineSegment(sketch, "E377", {"start": v(129.25, -56.25) * mm, "end": v(129.25, -59.75) * mm});
            skLineSegment(sketch, "E378", {"start": v(129.25, -59.75) * mm, "end": v(140.75, -59.75) * mm});
            skLineSegment(sketch, "E379", {"start": v(140.75, -59.75) * mm, "end": v(140.75, -56.25) * mm});
            skLineSegment(sketch, "E380", {"start": v(128.75, -56.25) * mm, "end": v(117.25, -56.25) * mm});
            skLineSegment(sketch, "E381", {"start": v(117.25, -56.25) * mm, "end": v(117.25, -59.75) * mm});
            skLineSegment(sketch, "E382", {"start": v(117.25, -59.75) * mm, "end": v(128.75, -59.75) * mm});
            skLineSegment(sketch, "E383", {"start": v(128.75, -59.75) * mm, "end": v(128.75, -56.25) * mm});
            skLineSegment(sketch, "E384", {"start": v(116.75, -56.25) * mm, "end": v(105.25, -56.25) * mm});
            skLineSegment(sketch, "E385", {"start": v(105.25, -56.25) * mm, "end": v(105.25, -59.75) * mm});
            skLineSegment(sketch, "E386", {"start": v(105.25, -59.75) * mm, "end": v(116.75, -59.75) * mm});
            skLineSegment(sketch, "E387", {"start": v(116.75, -59.75) * mm, "end": v(116.75, -56.25) * mm});
            skLineSegment(sketch, "E388", {"start": v(104.75, -56.25) * mm, "end": v(93.25, -56.25) * mm});
            skLineSegment(sketch, "E389", {"start": v(93.25, -56.25) * mm, "end": v(93.25, -59.75) * mm});
            skLineSegment(sketch, "E390", {"start": v(93.25, -59.75) * mm, "end": v(104.75, -59.75) * mm});
            skLineSegment(sketch, "E391", {"start": v(104.75, -59.75) * mm, "end": v(104.75, -56.25) * mm});
            skLineSegment(sketch, "E392", {"start": v(92.75, -56.25) * mm, "end": v(81.25, -56.25) * mm});
            skLineSegment(sketch, "E393", {"start": v(81.25, -56.25) * mm, "end": v(81.25, -59.75) * mm});
            skLineSegment(sketch, "E394", {"start": v(81.25, -59.75) * mm, "end": v(92.75, -59.75) * mm});
            skLineSegment(sketch, "E395", {"start": v(92.75, -59.75) * mm, "end": v(92.75, -56.25) * mm});
            skLineSegment(sketch, "E396", {"start": v(80.75, -56.25) * mm, "end": v(69.25, -56.25) * mm});
            skLineSegment(sketch, "E397", {"start": v(69.25, -56.25) * mm, "end": v(69.25, -59.75) * mm});
            skLineSegment(sketch, "E398", {"start": v(69.25, -59.75) * mm, "end": v(80.75, -59.75) * mm});
            skLineSegment(sketch, "E399", {"start": v(80.75, -59.75) * mm, "end": v(80.75, -56.25) * mm});
            skLineSegment(sketch, "E400", {"start": v(68.75, -56.25) * mm, "end": v(57.25, -56.25) * mm});
            skLineSegment(sketch, "E401", {"start": v(57.25, -56.25) * mm, "end": v(57.25, -59.75) * mm});
            skLineSegment(sketch, "E402", {"start": v(57.25, -59.75) * mm, "end": v(68.75, -59.75) * mm});
            skLineSegment(sketch, "E403", {"start": v(68.75, -59.75) * mm, "end": v(68.75, -56.25) * mm});
            skLineSegment(sketch, "E404", {"start": v(56.75, -56.25) * mm, "end": v(45.25, -56.25) * mm});
            skLineSegment(sketch, "E405", {"start": v(45.25, -56.25) * mm, "end": v(45.25, -59.75) * mm});
            skLineSegment(sketch, "E406", {"start": v(45.25, -59.75) * mm, "end": v(56.75, -59.75) * mm});
            skLineSegment(sketch, "E407", {"start": v(56.75, -59.75) * mm, "end": v(56.75, -56.25) * mm});
            skLineSegment(sketch, "E408", {"start": v(44.75, -56.25) * mm, "end": v(33.25, -56.25) * mm});
            skLineSegment(sketch, "E409", {"start": v(33.25, -56.25) * mm, "end": v(33.25, -59.75) * mm});
            skLineSegment(sketch, "E410", {"start": v(33.25, -59.75) * mm, "end": v(44.75, -59.75) * mm});
            skLineSegment(sketch, "E411", {"start": v(44.75, -59.75) * mm, "end": v(44.75, -56.25) * mm});
            skLineSegment(sketch, "E412", {"start": v(32.75, -56.25) * mm, "end": v(21.25, -56.25) * mm});
            skLineSegment(sketch, "E413", {"start": v(21.25, -56.25) * mm, "end": v(21.25, -59.75) * mm});
            skLineSegment(sketch, "E414", {"start": v(21.25, -59.75) * mm, "end": v(32.75, -59.75) * mm});
            skLineSegment(sketch, "E415", {"start": v(32.75, -59.75) * mm, "end": v(32.75, -56.25) * mm});
            skLineSegment(sketch, "E416", {"start": v(20.75, -56.25) * mm, "end": v(9.25, -56.25) * mm});
            skLineSegment(sketch, "E417", {"start": v(9.25, -56.25) * mm, "end": v(9.25, -59.75) * mm});
            skLineSegment(sketch, "E418", {"start": v(9.25, -59.75) * mm, "end": v(20.75, -59.75) * mm});
            skLineSegment(sketch, "E419", {"start": v(20.75, -59.75) * mm, "end": v(20.75, -56.25) * mm});
            skLineSegment(sketch, "E420", {"start": v(4, -67.75) * mm, "end": v(8.75, -67.75) * mm});
            skLineSegment(sketch, "E421", {"start": v(8.75, -67.75) * mm, "end": v(8.75, -64.25) * mm});
            skLineSegment(sketch, "E422", {"start": v(8.75, -64.25) * mm, "end": v(4, -64.25) * mm});
            skLineSegment(sketch, "E423", {"start": v(4, -71.75) * mm, "end": v(14.75, -71.75) * mm});
            skLineSegment(sketch, "E424", {"start": v(14.75, -71.75) * mm, "end": v(14.75, -68.25) * mm});
            skLineSegment(sketch, "E425", {"start": v(14.75, -68.25) * mm, "end": v(4, -68.25) * mm});
            skLineSegment(sketch, "E426", {"start": v(4, -63.75) * mm, "end": v(14.75, -63.75) * mm});
            skLineSegment(sketch, "E427", {"start": v(14.75, -63.75) * mm, "end": v(14.75, -60.25) * mm});
            skLineSegment(sketch, "E428", {"start": v(14.75, -60.25) * mm, "end": v(4, -60.25) * mm});
            skLineSegment(sketch, "E429", {"start": v(4, -59.75) * mm, "end": v(8.75, -59.75) * mm});
            skLineSegment(sketch, "E430", {"start": v(8.75, -59.75) * mm, "end": v(8.75, -56.25) * mm});
            skLineSegment(sketch, "E431", {"start": v(8.75, -56.25) * mm, "end": v(4, -56.25) * mm});
            skLineSegment(sketch, "E432", {"start": v(157, -56.25) * mm, "end": v(153.25, -56.25) * mm});
            skLineSegment(sketch, "E433", {"start": v(153.25, -56.25) * mm, "end": v(153.25, -59.75) * mm});
            skLineSegment(sketch, "E434", {"start": v(153.25, -59.75) * mm, "end": v(157, -59.75) * mm});
            skLineSegment(sketch, "E435", {"start": v(157, -60.25) * mm, "end": v(147.25, -60.25) * mm});
            skLineSegment(sketch, "E436", {"start": v(147.25, -60.25) * mm, "end": v(147.25, -63.75) * mm});
            skLineSegment(sketch, "E437", {"start": v(147.25, -63.75) * mm, "end": v(157, -63.75) * mm});
            skLineSegment(sketch, "E438", {"start": v(157, -64.25) * mm, "end": v(153.25, -64.25) * mm});
            skLineSegment(sketch, "E439", {"start": v(153.25, -64.25) * mm, "end": v(153.25, -67.75) * mm});
            skLineSegment(sketch, "E440", {"start": v(153.25, -67.75) * mm, "end": v(157, -67.75) * mm});
            skLineSegment(sketch, "E441", {"start": v(157, -68.25) * mm, "end": v(147.25, -68.25) * mm});
            skLineSegment(sketch, "E442", {"start": v(147.25, -68.25) * mm, "end": v(147.25, -71.75) * mm});
            skLineSegment(sketch, "E443", {"start": v(147.25, -71.75) * mm, "end": v(157, -71.75) * mm});
            skSolve(sketch);
        }
        {
            var Q0;
            {var subQ0=sQuery(id+"F0.wireOp",EDGE,"E1");var subQ1=sQuery(id+"F0.wireOp",EDGE,"E0");var subQ2=makeQuery(id+"F0.imprint","INTERSECT",VERTEX,{"derivedFrom":[subQ1,subQ0]});Q0=makeQuery(id+"F0.imprint","IMPRINT",FACE,{"disambiguationData":[TD([[makeQuery(id+"F0.imprint","IMPRINT",EDGE,{"disambiguationData":[TD([[subQ2,-1.0]])],"derivedFrom":subQ1}),1.0]])]});}
            var Q1;
            {var subQ0=sQuery(id+"F0.wireOp",EDGE,"E3");var subQ1=sQuery(id+"F0.wireOp",EDGE,"E1");var subQ2=makeQuery(id+"F0.imprint","INTERSECT",VERTEX,{"derivedFrom":[subQ1,subQ0]});Q1=makeQuery(id+"F0.imprint","IMPRINT",FACE,{"disambiguationData":[TD([[makeQuery(id+"F0.imprint","IMPRINT",EDGE,{"disambiguationData":[TD([[subQ2,1.0]])],"derivedFrom":subQ1}),-1.0]])]});}
            var Q2;
            {var subQ0=sQuery(id+"F0.wireOp",EDGE,"E3");var subQ1=sQuery(id+"F0.wireOp",EDGE,"E2");var subQ2=makeQuery(id+"F0.imprint","INTERSECT",VERTEX,{"derivedFrom":[subQ1,subQ0]});Q2=makeQuery(id+"F0.imprint","IMPRINT",FACE,{"disambiguationData":[TD([[makeQuery(id+"F0.imprint","IMPRINT",EDGE,{"disambiguationData":[TD([[subQ2,1.0]])],"derivedFrom":subQ1}),1.0]])]});}
            var Q3;
            {var subQ0=sQuery(id+"F0.wireOp",EDGE,"E2");var subQ1=sQuery(id+"F0.wireOp",EDGE,"E0");var subQ2=makeQuery(id+"F0.imprint","INTERSECT",VERTEX,{"derivedFrom":[subQ1,subQ0]});Q3=makeQuery(id+"F0.imprint","IMPRINT",FACE,{"disambiguationData":[TD([[makeQuery(id+"F0.imprint","IMPRINT",EDGE,{"disambiguationData":[TD([[subQ2,1.0]])],"derivedFrom":subQ1}),1.0]])]});}
            extrude(context, id + "F1", {"entities" : qUnion([Q0, Q1, Q2, Q3]), "oppositeDirection" : true, "depth" : 220 * mm, "offsetDistance" : 25 * mm});
        }
        {
            var Q0;
            {var subQ1=sQuery(id+"F0.wireOp",EDGE,"E10");Q0=makeQuery(id+"F0.imprint","IMPRINT",FACE,{"disambiguationData":[TD([[makeQuery(id+"F0.imprint","IMPRINT",EDGE,{"derivedFrom":subQ1}),-1.0]])]});}
            var Q1;
            {var subQ0=sQuery(id+"F0.wireOp",EDGE,"E9");Q1=makeQuery(id+"F0.imprint","IMPRINT",FACE,{"disambiguationData":[TD([[makeQuery(id+"F0.imprint","IMPRINT",EDGE,{"derivedFrom":subQ0}),-1.0]])]});}
            var Q2;
            {var subQ1=sQuery(id+"F0.wireOp",EDGE,"E8");Q2=makeQuery(id+"F0.imprint","IMPRINT",FACE,{"disambiguationData":[TD([[makeQuery(id+"F0.imprint","IMPRINT",EDGE,{"derivedFrom":subQ1}),-1.0]])]});}
            var Q3;
            {var subQ3=sQuery(id+"F0.wireOp",EDGE,"E4");Q3=makeQuery(id+"F0.imprint","IMPRINT",FACE,{"disambiguationData":[TD([[makeQuery(id+"F0.imprint","IMPRINT",EDGE,{"derivedFrom":subQ3}),-1.0]])]});}
            var Q4;
            {var subQ1=sQuery(id+"F0.wireOp",EDGE,"E4");Q4=makeQuery(id+"F0.imprint","IMPRINT",FACE,{"disambiguationData":[TD([[makeQuery(id+"F0.imprint","IMPRINT",EDGE,{"derivedFrom":subQ1}),1.0]])]});}
            var Q5;
            {var subQ2=sQuery(id+"F0.wireOp",EDGE,"E5");Q5=makeQuery(id+"F0.imprint","IMPRINT",FACE,{"disambiguationData":[TD([[makeQuery(id+"F0.imprint","IMPRINT",EDGE,{"derivedFrom":subQ2}),1.0]])]});}
            var Q6;
            {var subQ0=sQuery(id+"F0.wireOp",EDGE,"E6");Q6=makeQuery(id+"F0.imprint","IMPRINT",FACE,{"disambiguationData":[TD([[makeQuery(id+"F0.imprint","IMPRINT",EDGE,{"derivedFrom":subQ0}),1.0]])]});}
            var Q7;
            {var subQ4=sQuery(id+"F0.wireOp",EDGE,"E7");Q7=makeQuery(id+"F0.imprint","IMPRINT",FACE,{"disambiguationData":[TD([[makeQuery(id+"F0.imprint","IMPRINT",EDGE,{"derivedFrom":subQ4}),1.0]])]});}
            var Q8;
            {var subQ8=sQuery(id+"F0.wireOp",EDGE,"E25");var subQ9=sQuery(id+"F0.wireOp",EDGE,"E0");var subQ10=makeQuery(id+"F0.imprint","INTERSECT",VERTEX,{"derivedFrom":[subQ9,subQ8]});Q8=makeQuery(id+"F0.imprint","IMPRINT",FACE,{"disambiguationData":[TD([[makeQuery(id+"F0.imprint","IMPRINT",EDGE,{"disambiguationData":[TD([[subQ10,1.0]])],"derivedFrom":subQ9}),1.0]])]});}
            var Q9;
            {var subQ0=sQuery(id+"F0.wireOp",EDGE,"E23");var subQ14=sQuery(id+"F0.wireOp",EDGE,"E0");var subQ15=makeQuery(id+"F0.imprint","INTERSECT",VERTEX,{"derivedFrom":[subQ14,subQ0]});Q9=makeQuery(id+"F0.imprint","IMPRINT",FACE,{"disambiguationData":[TD([[makeQuery(id+"F0.imprint","IMPRINT",EDGE,{"disambiguationData":[TD([[subQ15,-1.0]])],"derivedFrom":subQ14}),1.0]])]});}
            var Q10;
            {var subQ0=sQuery(id+"F0.wireOp",EDGE,"E22");var subQ8=sQuery(id+"F0.wireOp",EDGE,"E0");var subQ9=makeQuery(id+"F0.imprint","INTERSECT",VERTEX,{"derivedFrom":[subQ8,subQ0]});Q10=makeQuery(id+"F0.imprint","IMPRINT",FACE,{"disambiguationData":[TD([[makeQuery(id+"F0.imprint","IMPRINT",EDGE,{"disambiguationData":[TD([[subQ9,1.0]])],"derivedFrom":subQ8}),1.0]])]});}
            extrude(context, id + "F2", {"entities" : qUnion([Q0, Q1, Q2, Q3, Q4, Q5, Q6, Q7, Q8, Q9, Q10]), "oppositeDirection" : true, "depth" : 6 * mm, "offsetDistance" : 25 * mm});
        }
        {
            var Q0;
            {var subQ1=sQuery(id+"F0.wireOp",EDGE,"E4");Q0=makeQuery(id+"F0.imprint","IMPRINT",FACE,{"disambiguationData":[TD([[makeQuery(id+"F0.imprint","IMPRINT",EDGE,{"derivedFrom":subQ1}),1.0]])]});}
            var sketch = newSketch(context, id + "F3", { "sketchPlane" : qUnion([Q0])});
            skLineSegment(sketch, "E444.bottom", {"start": v(4.03, -56.01) * mm, "end": v(157, -56.01) * mm});
            skLineSegment(sketch, "E444.top", {"start": v(4.03, -71.98) * mm, "end": v(157, -71.98) * mm});
            skLineSegment(sketch, "E444.left", {"start": v(4.03, -56.01) * mm, "end": v(4.03, -71.98) * mm});
            skLineSegment(sketch, "E444.right", {"start": v(157, -56.01) * mm, "end": v(157, -71.98) * mm});
            skSolve(sketch);
        }
        {
            var Q0;
            Q0=makeQuery(id+"F3.imprint","IMPRINT",FACE,{"disambiguationData":[TD([[makeQuery(id+"F3.imprint","IMPRINT",EDGE,{"derivedFrom":sQuery(id+"F3.wireOp",EDGE,"E444.bottom")}),-1.0]])]});
            extrude(context, id + "F4", {"entities" : qUnion([Q0]), "operationType" : NewBodyOperationType.ADD, "oppositeDirection" : true, "depth" : 6 * mm, "offsetDistance" : 25 * mm});
        }
        {
            var Q0;
            Q0=makeQuery(id+"F0.imprint","IMPRINT",FACE,{"disambiguationData":[TD([[makeQuery(id+"F0.imprint","IMPRINT",EDGE,{"derivedFrom":sQuery(id+"F0.wireOp",EDGE,"E236")}),-1.0]])]});
            extrude(context, id + "F5", {"entities" : qUnion([Q0]), "operationType" : NewBodyOperationType.REMOVE, "oppositeDirection" : true, "depth" : 1 * mm, "offsetDistance" : 25 * mm});
        }
        {
            var Q0;
            {var subQ1=sQuery(id+"F0.wireOp",EDGE,"E10");Q0=makeQuery(id+"F0.imprint","IMPRINT",FACE,{"disambiguationData":[TD([[makeQuery(id+"F0.imprint","IMPRINT",EDGE,{"derivedFrom":subQ1}),-1.0]])]});}
            var sketch = newSketch(context, id + "F6", { "sketchPlane" : qUnion([Q0])});
            skLineSegment(sketch, "E445.bottom", {"start": v(-156.96, -55.97) * mm, "end": v(-3.9, -55.97) * mm});
            skLineSegment(sketch, "E445.top", {"start": v(-156.96, -72.1) * mm, "end": v(-3.9, -72.1) * mm});
            skLineSegment(sketch, "E445.left", {"start": v(-156.96, -55.97) * mm, "end": v(-156.96, -72.1) * mm});
            skLineSegment(sketch, "E445.right", {"start": v(-3.9, -55.97) * mm, "end": v(-3.9, -72.1) * mm});
            skSolve(sketch);
        }
        {
            var Q0;
            {var subQ2=sQuery(id+"F6.wireOp",EDGE,"E445.top");Q0=makeQuery(id+"F6.imprint","IMPRINT",FACE,{"disambiguationData":[TD([[makeQuery(id+"F6.imprint","IMPRINT",EDGE,{"derivedFrom":subQ2}),1.0]])]});}
            extrude(context, id + "F7", {"entities" : qUnion([Q0]), "operationType" : NewBodyOperationType.ADD, "oppositeDirection" : true, "depth" : 6 * mm, "offsetDistance" : 25 * mm});
        }
        {
            var Q0;
            Q0=makeQuery(id+"F0.imprint","IMPRINT",FACE,{"disambiguationData":[TD([[makeQuery(id+"F0.imprint","IMPRINT",EDGE,{"derivedFrom":sQuery(id+"F0.wireOp",EDGE,"E26")}),1.0]])]});
            extrude(context, id + "F8", {"entities" : qUnion([Q0]), "operationType" : NewBodyOperationType.REMOVE, "oppositeDirection" : true, "depth" : 1 * mm, "offsetDistance" : 25 * mm});
        }
        {
            var Q0;
            Q0=makeQuery(id+"F1.opExtrude","SWEPT_FACE",FACE,{"disambiguationData":[OSD([sQuery(id+"F0.wireOp",EDGE,"E24")])]});
            var sketch = newSketch(context, id + "F9", { "sketchPlane" : qUnion([Q0])});
            skLineSegment(sketch, "E446.bottom", {"start": v(220, 72) * mm, "end": v(214, 72) * mm});
            skLineSegment(sketch, "E446.top", {"start": v(220, -72) * mm, "end": v(214, -72) * mm});
            skLineSegment(sketch, "E446.left", {"start": v(220, 72) * mm, "end": v(220, -72) * mm});
            skLineSegment(sketch, "E446.right", {"start": v(214, 72) * mm, "end": v(214, -72) * mm});
            skSolve(sketch);
        }
        {
            var Q0;
            Q0=makeQuery(id+"F9.imprint","IMPRINT",FACE,{"disambiguationData":[TD([[makeQuery(id+"F9.imprint","IMPRINT",EDGE,{"derivedFrom":sQuery(id+"F9.wireOp",EDGE,"E446.bottom")}),1.0]])]});
            extrude(context, id + "F10", {"entities" : qUnion([Q0]), "depth" : 328 * mm, "offsetDistance" : 25 * mm});
        }
        {
            var Q0;
            Q0=makeQuery(id+"F1.opExtrude","SWEPT_FACE",FACE,{"disambiguationData":[OSD([sQuery(id+"F0.wireOp",EDGE,"E1")])]});
            var sketch = newSketch(context, id + "F11", { "sketchPlane" : qUnion([Q0])});
            skLineSegment(sketch, "E447.bottom", {"start": v(-8.13, 63.84) * mm, "end": v(-211.87, 63.84) * mm});
            skLineSegment(sketch, "E447.top", {"start": v(-8.13, -63.84) * mm, "end": v(-211.87, -63.84) * mm});
            skLineSegment(sketch, "E447.left", {"start": v(-8.13, 63.84) * mm, "end": v(-8.13, -63.84) * mm});
            skLineSegment(sketch, "E447.right", {"start": v(-211.87, 63.84) * mm, "end": v(-211.87, -63.84) * mm});
            skPoint(sketch, "E447.middle", {"position": v(-110, 0) * mm});
            skPoint(sketch, "E447.middle.positionSnap0", {"position": v(-110, 72) * mm});
            skPoint(sketch, "E447.centerSnap0", {"position": v(-110, 72) * mm});
            skSolve(sketch);
        }
        {
            var Q0;
            Q0=makeQuery(id+"F11.imprint","IMPRINT",FACE,{"disambiguationData":[TD([[makeQuery(id+"F11.imprint","IMPRINT",EDGE,{"derivedFrom":sQuery(id+"F11.wireOp",EDGE,"E447.bottom")}),1.0]])]});
            extrude(context, id + "F12", {"entities" : qUnion([Q0]), "operationType" : NewBodyOperationType.REMOVE, "oppositeDirection" : true, "depth" : 1 * mm, "offsetDistance" : 25 * mm});
        }
        {
            var Q0;
            Q0=makeQuery(id+"F1.opExtrude","SWEPT_FACE",FACE,{"disambiguationData":[OSD([sQuery(id+"F0.wireOp",EDGE,"E1")])]});
            var sketch = newSketch(context, id + "F13", { "sketchPlane" : qUnion([Q0])});
            skArc(sketch, "E448", {"start": v(0, 72) * mm, "mid": v(-110, 119.93) * mm, "end": v(-220, 72) * mm});
            skSolve(sketch);
        }
        {
            var Q0;
            Q0=makeQuery(id+"F13.imprint","IMPRINT",FACE,{"disambiguationData":[TD([[makeQuery(id+"F13.imprint","IMPRINT",EDGE,{"derivedFrom":sQuery(id+"F13.wireOp",EDGE,"E448")}),1.0]])]});
            extrude(context, id + "F14", {"entities" : qUnion([Q0]), "oppositeDirection" : true, "depth" : 330 * mm, "offsetDistance" : 25 * mm});
        }
    });
